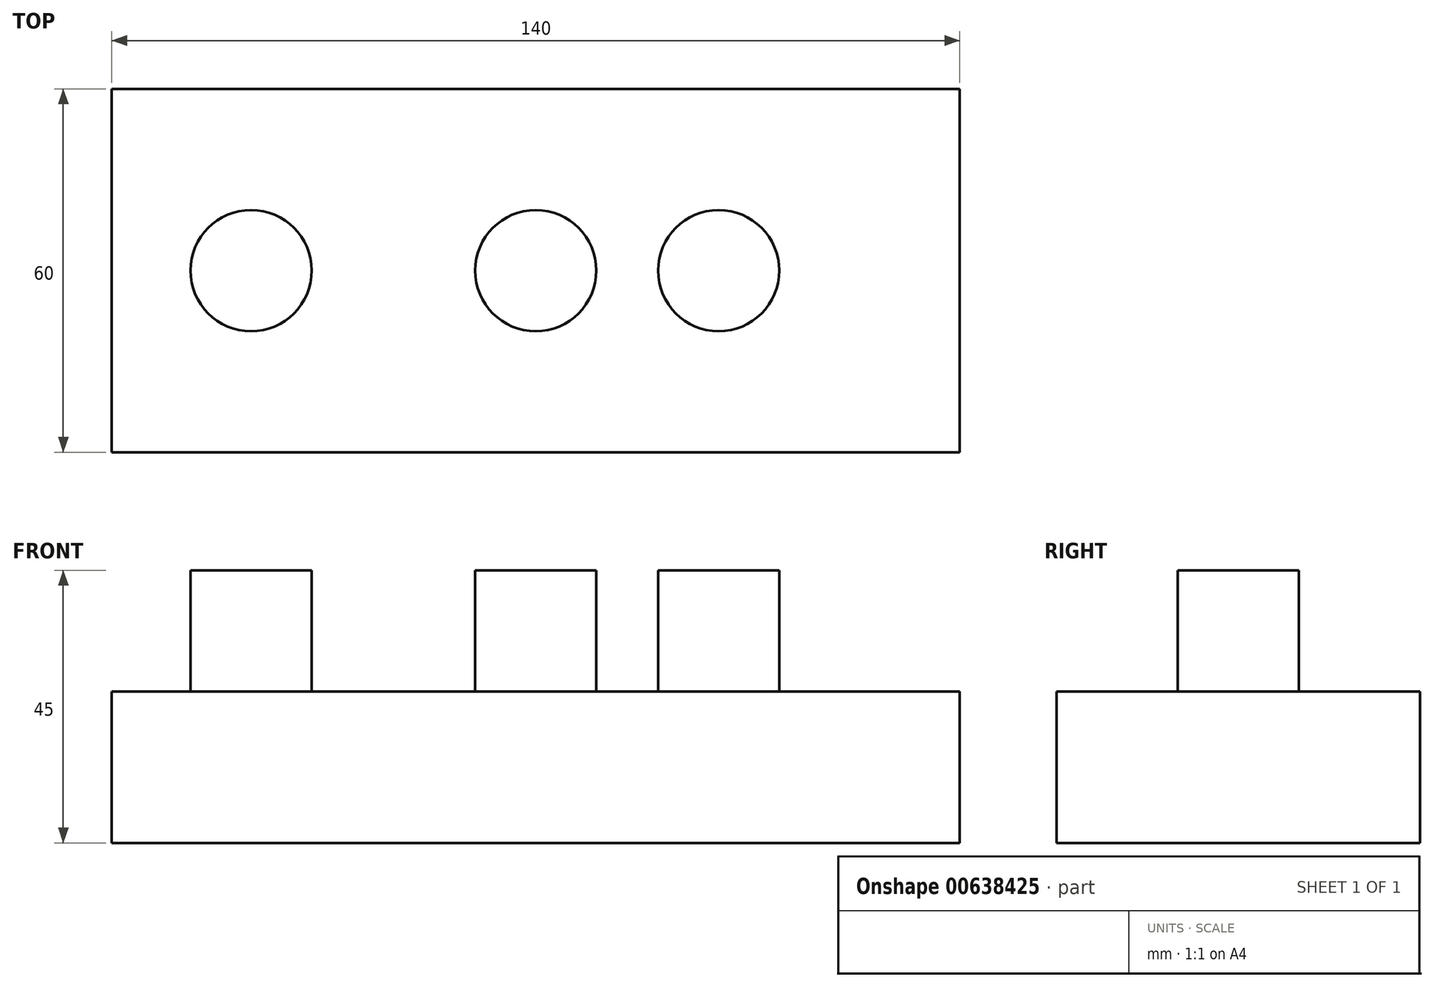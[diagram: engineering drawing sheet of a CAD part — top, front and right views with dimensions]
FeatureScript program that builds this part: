
annotation { "Feature Type Name" : "Feature", "Feature Type Description" : "" }
export const myFeature = defineFeature(function(context is Context, id is Id, definition is map)
    precondition{}
    {
        {
            var Q0;
            Q0=qCreatedBy(makeId("Top.planeOp"),FACE);
            var sketch = newSketch(context, id + "F0", { "sketchPlane" : qUnion([Q0])});
            skLineSegment(sketch, "E0.bottom", {"start": v(-70, 30) * mm, "end": v(70, 30) * mm});
            skLineSegment(sketch, "E0.top", {"start": v(-70, -30) * mm, "end": v(70, -30) * mm});
            skLineSegment(sketch, "E0.left", {"start": v(-70, 30) * mm, "end": v(-70, -30) * mm});
            skLineSegment(sketch, "E0.right", {"start": v(70, 30) * mm, "end": v(70, -30) * mm});
            skPoint(sketch, "E0.middle", {"position": v(0, 0) * mm});
            skSolve(sketch);
        }
        {
            var Q0;
            Q0=makeQuery(id+"F0.imprint","IMPRINT",FACE,{"disambiguationData":[TD([[makeQuery(id+"F0.imprint","IMPRINT",EDGE,{"derivedFrom":sQuery(id+"F0.wireOp",EDGE,"E0.bottom")}),-1.0]])]});
            extrude(context, id + "F1", {"entities" : qUnion([Q0]), "depth" : 25 * mm, "offsetDistance" : 25 * mm});
        }
        {
            var Q0;
            Q0=makeQuery(id+"F1.opExtrude","CAP_FACE",FACE,{"disambiguationData":[OSD([sQuery(id+"F0.wireOp",EDGE,"E0.bottom"),sQuery(id+"F0.wireOp",EDGE,"E0.top"),sQuery(id+"F0.wireOp",EDGE,"E0.left"),sQuery(id+"F0.wireOp",EDGE,"E0.right")])],"isStart":false});
            var sketch = newSketch(context, id + "F2", { "sketchPlane" : qUnion([Q0])});
            skCircle(sketch, "E1", {"center": v(-47, 0) * mm, "radius": 10 * mm});
            skSolve(sketch);
        }
        {
            var Q0;
            Q0=makeQuery(id+"F2.imprint","IMPRINT",FACE,{"disambiguationData":[TD([[makeQuery(id+"F2.imprint","IMPRINT",EDGE,{"derivedFrom":sQuery(id+"F2.wireOp",EDGE,"E1")}),-1.0]])]});
            var sketch = newSketch(context, id + "F3", { "sketchPlane" : qUnion([Q0])});
            skCircle(sketch, "E2", {"center": v(0, 0) * mm, "radius": 10 * mm});
            skSolve(sketch);
        }
        {
            var Q0;
            Q0=makeQuery(id+"F2.imprint","IMPRINT",FACE,{"disambiguationData":[TD([[makeQuery(id+"F2.imprint","IMPRINT",EDGE,{"derivedFrom":sQuery(id+"F2.wireOp",EDGE,"E1")}),-1.0]])]});
            var sketch = newSketch(context, id + "F4", { "sketchPlane" : qUnion([Q0])});
            skCircle(sketch, "E3", {"center": v(30.2, 0) * mm, "radius": 10 * mm});
            skSolve(sketch);
        }
        {
            var Q0;
            Q0=makeQuery(id+"F2.imprint","IMPRINT",FACE,{"disambiguationData":[TD([[makeQuery(id+"F2.imprint","IMPRINT",EDGE,{"derivedFrom":sQuery(id+"F2.wireOp",EDGE,"E1")}),1.0]])]});
            extrude(context, id + "F5", {"entities" : qUnion([Q0]), "operationType" : NewBodyOperationType.ADD, "depth" : 20 * mm, "offsetDistance" : 25 * mm});
        }
        {
            var Q0;
            Q0=makeQuery(id+"F3.imprint","IMPRINT",FACE,{"disambiguationData":[TD([[makeQuery(id+"F3.imprint","IMPRINT",EDGE,{"derivedFrom":sQuery(id+"F3.wireOp",EDGE,"E2")}),1.0]])]});
            extrude(context, id + "F6", {"entities" : qUnion([Q0]), "operationType" : NewBodyOperationType.ADD, "depth" : 20 * mm, "offsetDistance" : 25 * mm});
        }
        {
            var Q0;
            Q0=makeQuery(id+"F4.imprint","IMPRINT",FACE,{"disambiguationData":[TD([[makeQuery(id+"F4.imprint","IMPRINT",EDGE,{"derivedFrom":sQuery(id+"F4.wireOp",EDGE,"E3")}),1.0]])]});
            extrude(context, id + "F7", {"entities" : qUnion([Q0]), "operationType" : NewBodyOperationType.ADD, "depth" : 20 * mm, "offsetDistance" : 25 * mm});
        }
    });
